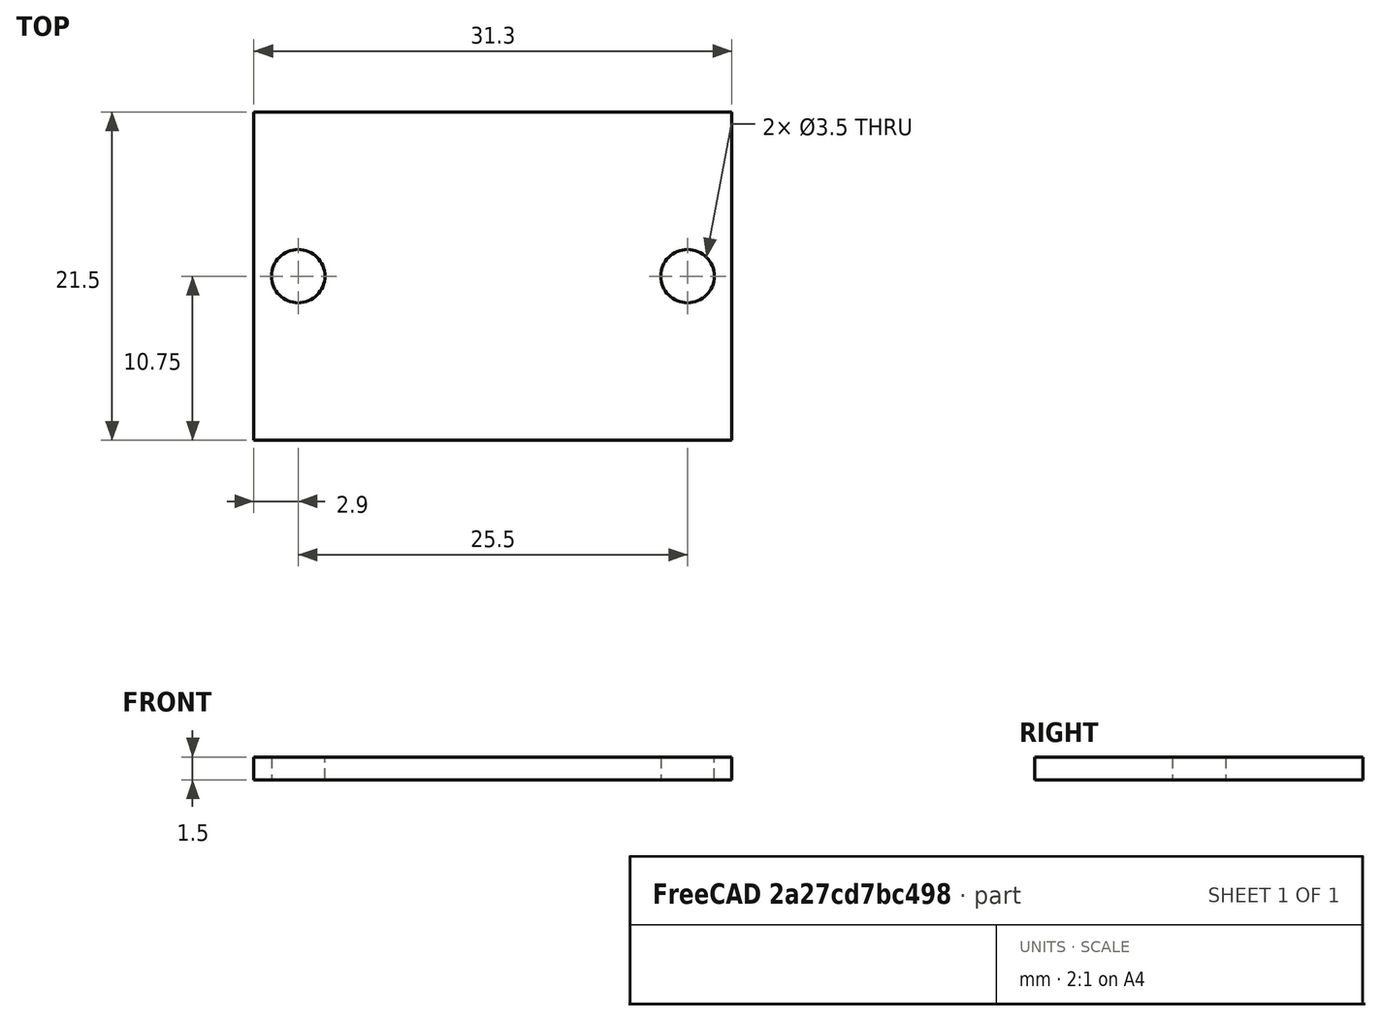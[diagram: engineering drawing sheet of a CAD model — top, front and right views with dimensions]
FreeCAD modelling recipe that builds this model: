
FCSTD DOCUMENT  (FreeCAD 0.20R29603 (Git))
Label: Multiplexer PCBA
License: All rights reserved
LicenseURL: http://en.wikipedia.org/wiki/All_rights_reserved
objects: Sketcher::SketchObject×1, PartDesign::Pad×1, PartDesign::Body×1, App::Part×1
note: 4 computed .brp shape members not serialized (recipe doc carries the construction recipe); baked Part::Feature solids carry a one-line shape summary decoded from their .brp

FEATURE [Sketcher::SketchObject] Sketch
  FullyConstrained = true
  MapMode = 5
  Support = -> [XY_Plane001]
  sketch-geometry (6):
    g0: LineSegment StartX=-15.65 StartY=10.75 StartZ=0 EndX=15.65 EndY=10.75 EndZ=0
    g1: LineSegment StartX=15.65 StartY=10.75 StartZ=0 EndX=15.65 EndY=-10.75 EndZ=0
    g2: LineSegment StartX=15.65 StartY=-10.75 StartZ=0 EndX=-15.65 EndY=-10.75 EndZ=0
    g3: LineSegment StartX=-15.65 StartY=-10.75 StartZ=0 EndX=-15.65 EndY=10.75 EndZ=0
    g4: Circle CenterX=-12.75 CenterY=0 CenterZ=0 NormalX=0 NormalY=0 NormalZ=1 AngleXU=0 Radius=1.75
    g5: Circle CenterX=12.75 CenterY=0 CenterZ=0 NormalX=0 NormalY=0 NormalZ=1 AngleXU=0 Radius=1.75
  constraints (18):
    c: Coincident(g0,g1)
    c: Coincident(g1,g2)
    c: Coincident(g2,g3)
    c: Coincident(g3,g0)
    c: Horizontal(g0)
    c: Horizontal(g2)
    c: Vertical(g1)
    c: Vertical(g3)
    c: DistanceX(g0,g0) = 31.3
    c: DistanceY(g3,g3) = 21.5
    c: DistanceY(g-1,g0) = 10.75
    c: DistanceX(g0,g-1) = 15.65
    c: DistanceX(g4,g5) = 25.5
    c: Horizontal(g4,g-1)
    c: Horizontal(g5,g-1)
    c: DistanceX(g4,g-1) = 12.75
    c: Equal(g4,g5)
    c: Diameter(g4) = 3.5
FEATURE [PartDesign::Pad] Pad
  Direction = (0,0,1)
  Length = 1.5
  Length2 = 10
  Profile = -> Sketch
  ReferenceAxis = -> Sketch [N_Axis]
  Type = 0
FEATURE [PartDesign::Body] Body
  Group = -> [Sketch,Pad]
  Origin = -> Origin001
  Tip = -> Pad
FEATURE [App::Part] Part
  Group = -> [Body]
  Origin = -> Origin
